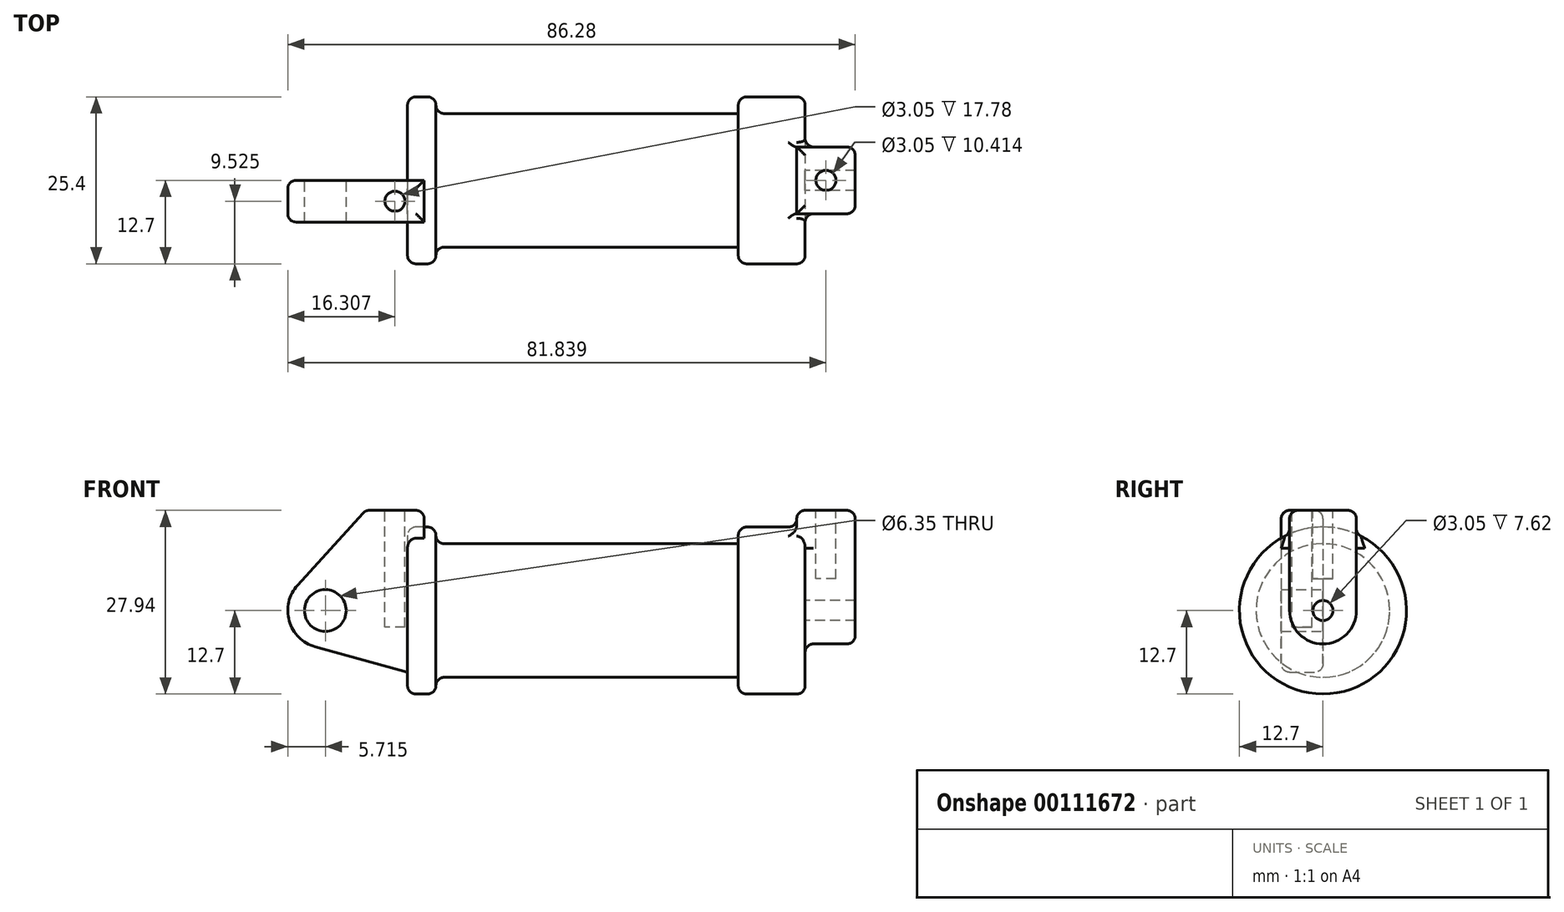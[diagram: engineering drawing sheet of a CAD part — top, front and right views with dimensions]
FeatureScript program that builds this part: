
annotation { "Feature Type Name" : "Feature", "Feature Type Description" : "" }
export const myFeature = defineFeature(function(context is Context, id is Id, definition is map)
    precondition{}
    {
        {
            var Q0;
            Q0=qCreatedBy(makeId("Front.planeOp"),FACE);
            var sketch = newSketch(context, id + "F0", { "sketchPlane" : qUnion([Q0])});
            skLineSegment(sketch, "E0", {"start": v(0, 0) * mm, "end": v(0, 12.7) * mm});
            skLineSegment(sketch, "E1", {"start": v(0, 12.7) * mm, "end": v(10.16, 12.7) * mm});
            skLineSegment(sketch, "E2", {"start": v(10.16, 12.7) * mm, "end": v(10.16, 10.16) * mm});
            skLineSegment(sketch, "E3", {"start": v(10.16, 10.16) * mm, "end": v(56.13, 10.16) * mm});
            skLineSegment(sketch, "E4", {"start": v(56.13, 10.16) * mm, "end": v(56.13, 12.7) * mm});
            skLineSegment(sketch, "E5", {"start": v(56.13, 12.7) * mm, "end": v(66.3, 12.7) * mm});
            skLineSegment(sketch, "E6", {"start": v(66.3, 12.7) * mm, "end": v(66.3, 0) * mm});
            skLineSegment(sketch, "E7", {"start": v(66.3, 0) * mm, "end": v(0, 0) * mm});
            skLineSegment(sketch, "E8", {"start": v(5.84, 15.24) * mm, "end": v(-0.5, 15.24) * mm});
            skLineSegment(sketch, "E9", {"start": v(-0.5, 15.24) * mm, "end": v(-10.88, 3.85) * mm});
            skLineSegment(sketch, "E10", {"start": v(0, 0) * mm, "end": v(-6.65, 0) * mm});
            skCircle(sketch, "E11", {"center": v(-6.65, 0) * mm, "radius": 5.72 * mm});
            skCircle(sketch, "E12", {"center": v(-6.65, 0) * mm, "radius": 3.18 * mm});
            skLineSegment(sketch, "E13", {"start": v(5.84, 15.24) * mm, "end": v(5.84, -9.4) * mm});
            skLineSegment(sketch, "E14", {"start": v(5.84, -9.4) * mm, "end": v(-8.18, -5.5) * mm});
            skSolve(sketch);
        }
        {
            var Q0;
            {var subQ0=sQuery(id+"F0.wireOp",EDGE,"E2");Q0=makeQuery(id+"F0.imprint","IMPRINT",FACE,{"disambiguationData":[TD([[makeQuery(id+"F0.imprint","IMPRINT",EDGE,{"derivedFrom":subQ0}),-1.0]])]});}
            var Q1;
            Q1=sQuery(id+"F0.wireOp",EDGE,"E7");
            revolve(context, id + "F1", {"entities" : qUnion([Q0]), "axis" : qUnion([Q1]), "revolveType" : RevolveType.FULL});
        }
        {
            var Q0;
            {var subQ3=sQuery(id+"F0.wireOp",EDGE,"E0");Q0=makeQuery(id+"F0.imprint","IMPRINT",FACE,{"disambiguationData":[TD([[makeQuery(id+"F0.imprint","IMPRINT",EDGE,{"derivedFrom":subQ3}),1.0]])]});}
            var Q1;
            {var subQ4=sQuery(id+"F0.wireOp",EDGE,"E12");Q1=makeQuery(id+"F0.imprint","IMPRINT",FACE,{"disambiguationData":[TD([[makeQuery(id+"F0.imprint","IMPRINT",EDGE,{"derivedFrom":subQ4}),-1.0]])]});}
            var Q2;
            {var subQ0=sQuery(id+"F0.wireOp",EDGE,"E14");Q2=makeQuery(id+"F0.imprint","IMPRINT",FACE,{"disambiguationData":[TD([[makeQuery(id+"F0.imprint","IMPRINT",EDGE,{"derivedFrom":subQ0}),-1.0]])]});}
            var Q3;
            {var subQ0=sQuery(id+"F0.wireOp",EDGE,"E0");Q3=makeQuery(id+"F0.imprint","IMPRINT",FACE,{"disambiguationData":[TD([[makeQuery(id+"F0.imprint","IMPRINT",EDGE,{"derivedFrom":subQ0}),-1.0]])]});}
            extrude(context, id + "F2", {"entities" : qUnion([Q0, Q1, Q2, Q3]), "operationType" : NewBodyOperationType.ADD, "depth" : 6.35 * mm});
        }
        {
            var Q0;
            Q0=makeQuery(id+"F1.opRevolve","SWEPT_FACE",FACE,{"disambiguationData":[OSD([sQuery(id+"F0.wireOp",EDGE,"E6")])]});
            var sketch = newSketch(context, id + "F3", { "sketchPlane" : qUnion([Q0])});
            skCircle(sketch, "E15", {"center": v(0, 0) * mm, "radius": 1.52 * mm});
            skCircle(sketch, "E16", {"center": v(0, 0) * mm, "radius": 5.08 * mm});
            skLineSegment(sketch, "E17", {"start": v(-5.08, 0) * mm, "end": v(-5.08, 15.24) * mm});
            skLineSegment(sketch, "E18", {"start": v(5.08, 0) * mm, "end": v(5.08, 15.24) * mm});
            skLineSegment(sketch, "E19", {"start": v(-5.08, 15.24) * mm, "end": v(5.08, 15.24) * mm});
            skSolve(sketch);
        }
        {
            var Q0;
            {var subQ0=sQuery(id+"F3.wireOp",EDGE,"E17");var subQ1=sQuery(id+"F3.wireOp",EDGE,"E16");var subQ2=makeQuery(id+"F3.imprint","INTERSECT",VERTEX,{"derivedFrom":[subQ1,subQ0]});Q0=makeQuery(id+"F3.imprint","IMPRINT",FACE,{"disambiguationData":[TD([[makeQuery(id+"F3.imprint","IMPRINT",EDGE,{"disambiguationData":[TD([[subQ2,1.0]])],"derivedFrom":subQ1}),-1.0]])]});}
            var Q1;
            {var subQ0=sQuery(id+"F3.wireOp",EDGE,"E19");Q1=makeQuery(id+"F3.imprint","IMPRINT",FACE,{"disambiguationData":[TD([[makeQuery(id+"F3.imprint","IMPRINT",EDGE,{"derivedFrom":subQ0}),-1.0]])]});}
            var Q2;
            Q2=makeQuery(id+"F3.imprint","IMPRINT",FACE,{"disambiguationData":[TD([[makeQuery(id+"F3.imprint","IMPRINT",EDGE,{"derivedFrom":sQuery(id+"F3.wireOp",EDGE,"E15")}),-1.0]])]});
            extrude(context, id + "F4", {"entities" : qUnion([Q0, Q1, Q2]), "operationType" : NewBodyOperationType.ADD, "depth" : 7.62 * mm});
        }
        {
            var Q0;
            Q0 = qSketchRegion(id + "F3", true);
            extrude(context, id + "F5", {"entities" : qUnion([Q0]), "operationType" : NewBodyOperationType.ADD, "oppositeDirection" : true, "depth" : 1.27 * mm});
        }
        {
            var Q0;
            Q0=makeQuery(id+"F2.opExtrude","SWEPT_FACE",FACE,{"disambiguationData":[OSD([sQuery(id+"F0.wireOp",EDGE,"E13")])]});
            extrude(context, id + "F6", {"entities" : qUnion([Q0]), "operationType" : NewBodyOperationType.ADD, "depth" : 2.54 * mm});
        }
        {
            var Q0;
            Q0=makeQuery(id+"F4.boolean.opBoolean","SPLIT",FACE,{"disambiguationData":[TD([makeQuery(id+"F4.opExtrude","SWEPT_FACE",FACE,{"disambiguationData":[OSD([sQuery(id+"F3.wireOp",EDGE,"E15")])]})])],"derivedFrom":makeQuery(id+"F1.opRevolve","SWEPT_FACE",FACE,{"disambiguationData":[OSD([sQuery(id+"F0.wireOp",EDGE,"E6")])]})});
            var Q1;
            Q1=makeQuery(id+"F1.opRevolve","SWEPT_FACE",FACE,{"disambiguationData":[OSD([sQuery(id+"F0.wireOp",EDGE,"E2")])]});
            extrude(context, id + "F7", {"entities" : qUnion([Q0]), "operationType" : NewBodyOperationType.ADD, "endBound" : BoundingType.UP_TO_SURFACE, "oppositeDirection" : true, "endBoundEntityFace" : qUnion([Q1]), "depth" : 25.4 * mm});
        }
        {
            var Q0;
            {var subQ0=sQuery(id+"F0.wireOp",EDGE,"E8");Q0=makeQuery(id+"F6.boolean.opBoolean","MERGE",FACE,{"derivedFrom":[makeQuery(id+"F2.opExtrude","SWEPT_FACE",FACE,{"disambiguationData":[OSD([subQ0])]}),makeQuery(id+"F6.opExtrude","SWEPT_FACE",FACE,{"disambiguationData":[OSD([subQ0,sQuery(id+"F0.wireOp",EDGE,"E13")])]})]});}
            var sketch = newSketch(context, id + "F8", { "sketchPlane" : qUnion([Q0])});
            skCircle(sketch, "E20", {"center": v(3.94, -3.18) * mm, "radius": 1.52 * mm});
            skPoint(sketch, "E20.centerSnap0", {"position": v(3.94, -6.35) * mm});
            skPoint(sketch, "E20.centerSnap1", {"position": v(8.38, -3.18) * mm});
            skSolve(sketch);
        }
        {
            var Q0;
            Q0=makeQuery(id+"F8.imprint","IMPRINT",FACE,{"disambiguationData":[TD([[makeQuery(id+"F8.imprint","IMPRINT",EDGE,{"derivedFrom":sQuery(id+"F8.wireOp",EDGE,"E20")}),1.0]])]});
            extrude(context, id + "F9", {"entities" : qUnion([Q0]), "operationType" : NewBodyOperationType.REMOVE, "oppositeDirection" : true, "depth" : 17.78 * mm});
        }
        {
            var Q0;
            {var subQ0=sQuery(id+"F3.wireOp",EDGE,"E19");Q0=makeQuery(id+"F5.boolean.opBoolean","MERGE",FACE,{"derivedFrom":[makeQuery(id+"F4.opExtrude","SWEPT_FACE",FACE,{"disambiguationData":[OSD([subQ0])]}),makeQuery(id+"F5.opExtrude","SWEPT_FACE",FACE,{"disambiguationData":[OSD([subQ0])]})]});}
            var sketch = newSketch(context, id + "F10", { "sketchPlane" : qUnion([Q0])});
            skCircle(sketch, "E21", {"center": v(69.47, 0) * mm, "radius": 1.52 * mm});
            skPoint(sketch, "E21.centerSnap0", {"position": v(69.47, -5.08) * mm});
            skPoint(sketch, "E21.centerSnap1", {"position": v(73.91, 0) * mm});
            skSolve(sketch);
        }
        {
            var Q0;
            Q0=makeQuery(id+"F10.imprint","IMPRINT",FACE,{"disambiguationData":[TD([[makeQuery(id+"F10.imprint","IMPRINT",EDGE,{"derivedFrom":sQuery(id+"F10.wireOp",EDGE,"E21")}),1.0]])]});
            extrude(context, id + "F11", {"entities" : qUnion([Q0]), "operationType" : NewBodyOperationType.REMOVE, "oppositeDirection" : true, "depth" : 10.4 * mm});
        }
        {
            var Q0;
            Q0=makeQuery(id+"F1.opRevolve","SWEPT_EDGE",EDGE,{"disambiguationData":[OSD([sQuery(id+"F0.wireOp",EDGE,"E2"),sQuery(id+"F0.wireOp",EDGE,"E3")])]});
            var Q1;
            Q1=makeQuery(id+"F1.opRevolve","SWEPT_EDGE",EDGE,{"disambiguationData":[OSD([sQuery(id+"F0.wireOp",EDGE,"E4"),sQuery(id+"F0.wireOp",EDGE,"E5")])]});
            var Q2;
            Q2=makeQuery(id+"F4.boolean.opBoolean","SPLIT",EDGE,{"disambiguationData":[OD(1.0)],"derivedFrom":makeQuery(id+"F1.opRevolve","SWEPT_EDGE",EDGE,{"disambiguationData":[OSD([sQuery(id+"F0.wireOp",EDGE,"E5"),sQuery(id+"F0.wireOp",EDGE,"E6")])]})});
            var Q3;
            Q3=makeQuery(id+"F2.boolean.opBoolean","SPLIT",EDGE,{"disambiguationData":[OD(0.0)],"derivedFrom":makeQuery(id+"F1.opRevolve","SWEPT_EDGE",EDGE,{"disambiguationData":[OSD([sQuery(id+"F0.wireOp",EDGE,"E1"),sQuery(id+"F0.wireOp",EDGE,"E13")])]})});
            var Q4;
            Q4=makeQuery(id+"F1.opRevolve","SWEPT_EDGE",EDGE,{"disambiguationData":[OSD([sQuery(id+"F0.wireOp",EDGE,"E1"),sQuery(id+"F0.wireOp",EDGE,"E2")])]});
            fillet(context, id + "F12", {"entities" : qUnion([Q0, Q1, Q2, Q3, Q4]), "radius" : 1.27 * mm, "tangentPropagation" : true, "allowEdgeOverflow" : false});
        }
        {
            var Q0;
            Q0=makeQuery(id+"F4.opExtrude","CAP_EDGE",EDGE,{"disambiguationData":[OSD([sQuery(id+"F3.wireOp",EDGE,"E17")])],"isStart":false});
            var Q1;
            Q1=makeQuery(id+"F4.opExtrude","CAP_EDGE",EDGE,{"disambiguationData":[OSD([sQuery(id+"F3.wireOp",EDGE,"E16")])],"isStart":false});
            var Q2;
            Q2=makeQuery(id+"F4.opExtrude","CAP_EDGE",EDGE,{"disambiguationData":[OSD([sQuery(id+"F3.wireOp",EDGE,"E18")])],"isStart":false});
            var Q3;
            Q3=makeQuery(id+"F4.opExtrude","CAP_EDGE",EDGE,{"disambiguationData":[OSD([sQuery(id+"F3.wireOp",EDGE,"E19")])],"isStart":false});
            var Q4;
            {var subQ0=sQuery(id+"F3.wireOp",EDGE,"E19");var subQ1=sQuery(id+"F3.wireOp",EDGE,"E17");Q4=makeQuery(id+"F5.boolean.opBoolean","MERGE",EDGE,{"derivedFrom":[makeQuery(id+"F4.opExtrude","SWEPT_EDGE",EDGE,{"disambiguationData":[OSD([subQ1,subQ0])]}),makeQuery(id+"F5.opExtrude","SWEPT_EDGE",EDGE,{"disambiguationData":[OSD([subQ1,subQ0])]})]});}
            var Q5;
            Q5=makeQuery(id+"F5.opExtrude","CAP_EDGE",EDGE,{"disambiguationData":[OSD([sQuery(id+"F3.wireOp",EDGE,"E19")])],"isStart":false});
            var Q6;
            {var subQ0=sQuery(id+"F3.wireOp",EDGE,"E19");var subQ1=sQuery(id+"F3.wireOp",EDGE,"E18");Q6=makeQuery(id+"F5.boolean.opBoolean","MERGE",EDGE,{"derivedFrom":[makeQuery(id+"F4.opExtrude","SWEPT_EDGE",EDGE,{"disambiguationData":[OSD([subQ1,subQ0])]}),makeQuery(id+"F5.opExtrude","SWEPT_EDGE",EDGE,{"disambiguationData":[OSD([subQ1,subQ0])]})]});}
            var Q7;
            {var subQ0=sQuery(id+"F3.wireOp",EDGE,"E17");Q7=makeQuery(id+"F12.opFillet","BLEND_EDGE",EDGE,{"blendedFrom":[makeQuery(id+"F4.boolean.opBoolean","SPLIT",EDGE,{"disambiguationData":[OD(1.0)],"derivedFrom":makeQuery(id+"F1.opRevolve","SWEPT_EDGE",EDGE,{"disambiguationData":[OSD([sQuery(id+"F0.wireOp",EDGE,"E5"),sQuery(id+"F0.wireOp",EDGE,"E6")])]})}),makeQuery(id+"F5.boolean.opBoolean","MERGE",FACE,{"derivedFrom":[makeQuery(id+"F4.opExtrude","SWEPT_FACE",FACE,{"disambiguationData":[OSD([subQ0])]}),makeQuery(id+"F5.opExtrude","SWEPT_FACE",FACE,{"disambiguationData":[OSD([subQ0])]})]})],"blendedInto":[makeQuery(id+"F5.boolean.opBoolean","MERGE",FACE,{"derivedFrom":[makeQuery(id+"F4.opExtrude","SWEPT_FACE",FACE,{"disambiguationData":[OSD([subQ0])]}),makeQuery(id+"F5.opExtrude","SWEPT_FACE",FACE,{"disambiguationData":[OSD([subQ0])]})]})]});}
            var Q8;
            {var subQ0=sQuery(id+"F3.wireOp",EDGE,"E17");var subQ1=sQuery(id+"F3.wireOp",EDGE,"E16");Q8=makeQuery(id+"F4.boolean.opBoolean","SPLIT",EDGE,{"disambiguationData":[TD([makeQuery(id+"F4.opExtrude","SWEPT_FACE",FACE,{"disambiguationData":[OSD([subQ1])]})])],"derivedFrom":makeQuery(id+"F4.opExtrude","CAP_EDGE",EDGE,{"disambiguationData":[OSD([subQ0])],"isStart":true})});}
            var Q9;
            Q9=makeQuery(id+"F5.boolean.opBoolean","INTERSECT",EDGE,{"derivedFrom":[makeQuery(id+"F1.opRevolve","SWEPT_FACE",FACE,{"disambiguationData":[OSD([sQuery(id+"F0.wireOp",EDGE,"E5")])]}),makeQuery(id+"F5.opExtrude","CAP_FACE",FACE,{"disambiguationData":[OSD([sQuery(id+"F3.wireOp",EDGE,"E15"),sQuery(id+"F3.wireOp",EDGE,"E16"),sQuery(id+"F3.wireOp",EDGE,"E17"),sQuery(id+"F3.wireOp",EDGE,"E18"),sQuery(id+"F3.wireOp",EDGE,"E19")])],"isStart":false})]});
            fillet(context, id + "F13", {"entities" : qUnion([Q0, Q1, Q2, Q3, Q4, Q5, Q6, Q7, Q8, Q9]), "radius" : 1.27 * mm, "tangentPropagation" : true, "allowEdgeOverflow" : false});
        }
        {
            var Q0;
            Q0=makeQuery(id+"F6.opExtrude","CAP_EDGE",EDGE,{"disambiguationData":[OSD([sQuery(id+"F0.wireOp",EDGE,"E1"),sQuery(id+"F0.wireOp",EDGE,"E13")])],"isStart":false});
            var Q1;
            Q1=makeQuery(id+"F6.opExtrude","CAP_EDGE",EDGE,{"disambiguationData":[OSD([sQuery(id+"F0.wireOp",EDGE,"E8"),sQuery(id+"F0.wireOp",EDGE,"E13")])],"isStart":false});
            var Q2;
            {var subQ0=sQuery(id+"F0.wireOp",EDGE,"E13");var subQ1=sQuery(id+"F0.wireOp",EDGE,"E8");Q2=makeQuery(id+"F6.boolean.opBoolean","MERGE",EDGE,{"derivedFrom":[makeQuery(id+"F2.opExtrude","CAP_EDGE",EDGE,{"disambiguationData":[OSD([subQ1])],"isStart":true}),makeQuery(id+"F6.opExtrude","SWEPT_EDGE",EDGE,{"disambiguationData":[OSD([subQ1,subQ0]),TDD([makeQuery(id+"F2.opExtrude","CAP_VERTEX",VERTEX,{"disambiguationData":[OSD([subQ1,subQ0])],"isStart":true})])]})]});}
            var Q3;
            Q3=makeQuery(id+"F2.opExtrude","CAP_EDGE",EDGE,{"disambiguationData":[OSD([sQuery(id+"F0.wireOp",EDGE,"E9")])],"isStart":true});
            var Q4;
            Q4=makeQuery(id+"F2.opExtrude","CAP_EDGE",EDGE,{"disambiguationData":[OSD([sQuery(id+"F0.wireOp",EDGE,"E9")])],"isStart":false});
            var Q5;
            {var subQ0=sQuery(id+"F0.wireOp",EDGE,"E13");var subQ1=sQuery(id+"F0.wireOp",EDGE,"E8");Q5=makeQuery(id+"F6.boolean.opBoolean","MERGE",EDGE,{"derivedFrom":[makeQuery(id+"F2.opExtrude","CAP_EDGE",EDGE,{"disambiguationData":[OSD([subQ1])],"isStart":false}),makeQuery(id+"F6.opExtrude","SWEPT_EDGE",EDGE,{"disambiguationData":[OSD([subQ1,subQ0]),TDD([makeQuery(id+"F2.opExtrude","CAP_VERTEX",VERTEX,{"disambiguationData":[OSD([subQ1,subQ0])],"isStart":false})])]})]});}
            var Q6;
            Q6=makeQuery(id+"F2.opExtrude","SWEPT_EDGE",EDGE,{"disambiguationData":[OSD([sQuery(id+"F0.wireOp",EDGE,"E8"),sQuery(id+"F0.wireOp",EDGE,"E9")])]});
            var Q7;
            Q7=makeQuery(id+"F2.opExtrude","SWEPT_EDGE",EDGE,{"disambiguationData":[OSD([sQuery(id+"F0.wireOp",EDGE,"E9"),sQuery(id+"F0.wireOp",EDGE,"E11")])]});
            var Q8;
            Q8=makeQuery(id+"F2.opExtrude","SWEPT_EDGE",EDGE,{"disambiguationData":[OSD([sQuery(id+"F0.wireOp",EDGE,"E11"),sQuery(id+"F0.wireOp",EDGE,"E14")])]});
            fillet(context, id + "F14", {"entities" : qUnion([Q0, Q1, Q2, Q3, Q4, Q5, Q6, Q7, Q8]), "radius" : 1.27 * mm, "tangentPropagation" : true, "allowEdgeOverflow" : false});
        }
    });
